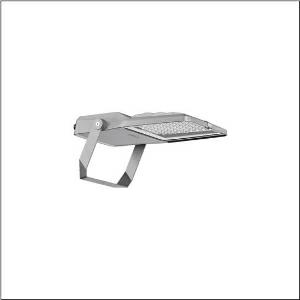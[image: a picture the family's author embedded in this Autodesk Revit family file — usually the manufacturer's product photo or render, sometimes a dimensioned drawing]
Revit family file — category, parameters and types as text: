
# Revit family: floodlight_fl_21_iq_mini___pl64_5xa7772b2e1a_9a08
name_source: partatom
category: Lighting Fixtures
units: mm (PartAtom-declared; Revit-internal decimal feet)

## family parameters
Cut with Voids When Loaded = No
Host = Face
Light Source = No
Part Type = Normal
Room Calculation Point = No
Round Connector Dimension = Use Diameter
Shared = No

## types (1)
- --- (1 x LED, 6020 lm, 45.5 W, 3000K)
    Apparent Load = 46 VA
    CIE Flux Codes = 28 80 98 100 100
    Color Rendering = 70
    Color Temperature = 3000K
    Default Elevation = 1800 mm
    Description = Floodlight FL 21 iQ mini, floodlight, primary light control with lens, of PMMA, primary optical cover: protective disc, of toughened safety glass, transparent, light distribution: PL64, light emission: direct distribution, installation type: surface-mounted, LED, High Power LED, rated luminous flux: 6.020lm, luminous efficacy: 132lm/W, light colour: 730, colour temperature: 3000K, control gear: iQ Street-Remote/DALI, control: Street-Remote, Auto-Match, Temp-Guard, Night-Set, Smart-Wire, Desk-Remote (wireless, voltage-free reading and setting of iQ features in the workshop via application-optimized NFC function/RFID function), optimised constant luminous flux control (CLO 2.0), with terminal, 6-pole, mains connection: 220..240V, AC, 50/60Hz, start of lifetime: 46W, end of service life: 48W, reduction: 22W, luminaire housing, of diecast aluminium, powder-coated, Siteco® metallic grey (DB 702S), corrosivity category C5 mid according to DIN EN ISO 12944, suitable for swimming pools, chlorine-resistant, sealing non-destructively replaceable, mounting bracket, of steel, galvanised, powder-coated, Siteco® metallic grey (DB 702S), protection rating (complete): IP66, insulation class (complete): insulation class II (safety insulation), certification: CE, ENEC, VDE, protection symbol: D, impact resistance: IK08, permissible operating ambient temperature: -40..+40°C, permissible operating ambient temperature for outdoor applications: -40..+50°C, standard: DIN EN 12944, LABS conformity tested according to VDMA 24364:2018-05, packaging unit: 1 piece

Light Distribution: PL64
    Height = 70 mm
    Lamp = 1 x LED
    Lamp Light Flux = 6020 lm
    Lamp Power = 45.5 W
    Lamp count = 1
    Length = 485 mm
    Luminous efficacy = 132 lm/W
    Manufacturer = Siteco
    ModVariant = No
    Model = 5XA7772B2E1A
    Number of Poles = 1
    OnlyDefault = Yes
    Power Factor = 1
    Product Name = Floodlight FL 21 iQ mini | PL64
    Product group = floodlight | pylon annexe
    ProductGroupID = 6200
    Protection Class = Protection class II
    Protection Degree = IP 66
    RLX_Detail_Level = 1
    RLX_Emergency_Light_Flux = 0 lm
    RLX_Emergency_Type = 0
    RLX_Emergency_Type_DB = No
    RlxData = <blob elided: 96169 chars, md5=d785e555>
    Socket = socket
    Standby Power = 0 W
    System Light Flux = 6020 lm
    System Power = 46 W
    Type Comments = factory setting: luminous flux: 100 % | dim-lin: 254 | 463 mA
    Type Image = l_1006845.jpg
    URL = http://relux.com
    VarID = @adj_166974
    Voltage = 0 V
    Weight = 0.00 kg
    Width = 337 mm

## geometry (parser evidence)
native form markers: Blend x4, Sweep x14
no freeform markers — native parametric forms only
